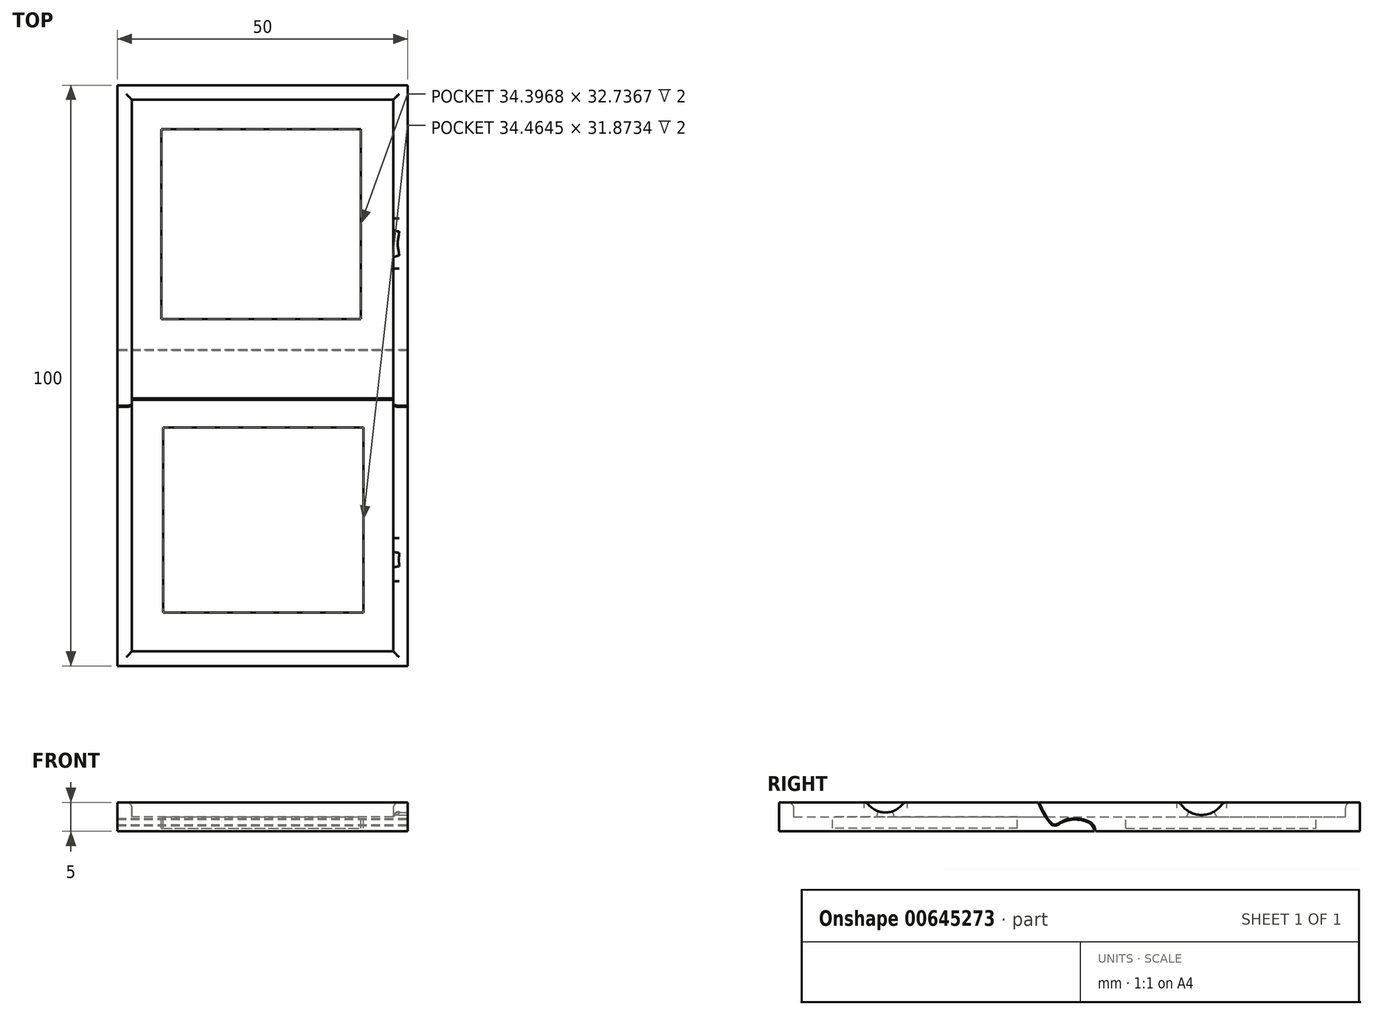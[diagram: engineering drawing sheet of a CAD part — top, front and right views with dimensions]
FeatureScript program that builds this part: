
annotation { "Feature Type Name" : "Feature", "Feature Type Description" : "" }
export const myFeature = defineFeature(function(context is Context, id is Id, definition is map)
    precondition{}
    {
        {
            var Q0;
            Q0=qCreatedBy(makeId("Front.planeOp"),FACE);
            var sketch = newSketch(context, id + "F0", { "sketchPlane" : qUnion([Q0])});
            skLineSegment(sketch, "E0.bottom", {"start": v(-50, 5) * mm, "end": v(0, 5) * mm});
            skLineSegment(sketch, "E0.top", {"start": v(-50, 0) * mm, "end": v(0, 0) * mm});
            skLineSegment(sketch, "E0.left", {"start": v(-50, 5) * mm, "end": v(-50, 0) * mm});
            skLineSegment(sketch, "E0.right", {"start": v(0, 5) * mm, "end": v(0, 0) * mm});
            skSolve(sketch);
        }
        {
            var Q0;
            Q0 = qSketchRegion(id + "F0", true);
            extrude(context, id + "F1", {"entities" : qUnion([Q0]), "endBound" : BoundingType.SYMMETRIC, "depth" : 100 * mm, "offsetDistance" : 25 * mm});
        }
        {
            var Q0;
            Q0=makeQuery(id+"F1.opExtrude","SWEPT_FACE",FACE,{"disambiguationData":[OSD([sQuery(id+"F0.wireOp",EDGE,"E0.bottom")])]});
            shell(context, id + "F2", {"entities" : qUnion([Q0]), "thickness" : 2.5 * mm});
        }
        {
            var Q0;
            Q0=makeQuery(id+"F1.opExtrude","SWEPT_FACE",FACE,{"disambiguationData":[OSD([sQuery(id+"F0.wireOp",EDGE,"E0.left")])]});
            var sketch = newSketch(context, id + "F3", { "sketchPlane" : qUnion([Q0])});
            skFitSpline(sketch, "E1", {"points": [v(-4.27, 0) * mm, v(0.38, 1.88) * mm, v(2.67, 1) * mm, v(5.4, 5) * mm], "startDerivative": vector(0, 15.13) * mm, "endDerivative": vector(6.53, 15.5) * mm});
            skFitSpline(sketch, "E2.0", {"points": [v(-4.45, 0) * mm, v(-4.45, 0.35) * mm, v(-4.26, 0.97) * mm, v(-3.57, 1.62) * mm, v(-2.63, 2.02) * mm, v(-1.56, 2.21) * mm, v(-0.48, 2.23) * mm, v(0.5, 2.07) * mm, v(1.25, 1.76) * mm, v(1.72, 1.48) * mm, v(2.04, 1.3) * mm, v(2.25, 1.2) * mm, v(2.43, 1.16) * mm, v(2.59, 1.15) * mm, v(2.76, 1.2) * mm, v(2.96, 1.32) * mm, v(3.18, 1.51) * mm, v(3.48, 1.84) * mm, v(3.88, 2.38) * mm, v(4.36, 3.2) * mm, v(4.82, 4.1) * mm, v(5.1, 4.75) * mm, v(5.24, 5.07) * mm]});
            skLineSegment(sketch, "E3", {"start": v(5.2, 5) * mm, "end": v(5.4, 5) * mm});
            skLineSegment(sketch, "E4", {"start": v(-4.45, 0) * mm, "end": v(-4.27, 0) * mm});
            skSolve(sketch);
        }
        {
            var Q0;
            Q0 = qSketchRegion(id + "F3", true);
            extrude(context, id + "F4", {"entities" : qUnion([Q0]), "operationType" : NewBodyOperationType.REMOVE, "oppositeDirection" : true, "depth" : 100 * mm, "offsetDistance" : 25 * mm});
        }
        {
            var Q0;
            {var subQ2=sQuery(id+"F0.wireOp",EDGE,"E0.top");Q0=makeQuery(id+"F4.boolean.opBoolean","SPLIT",FACE,{"disambiguationData":[TD([makeQuery(id+"F4.opExtrude","SWEPT_FACE",FACE,{"disambiguationData":[OSD([sQuery(id+"F3.wireOp",EDGE,"E1")])]})])],"derivedFrom":makeQuery(id+"F2.opShell","OFFSET_FACE",FACE,{"disambiguationData":[OSD([subQ2])]})});}
            var sketch = newSketch(context, id + "F5", { "sketchPlane" : qUnion([Q0])});
            skLineSegment(sketch, "E5.bottom", {"start": v(-42.12, -8.95) * mm, "end": v(-7.66, -8.95) * mm});
            skLineSegment(sketch, "E5.top", {"start": v(-42.12, -40.83) * mm, "end": v(-7.66, -40.83) * mm});
            skLineSegment(sketch, "E5.left", {"start": v(-42.12, -8.95) * mm, "end": v(-42.12, -40.83) * mm});
            skLineSegment(sketch, "E5.right", {"start": v(-7.66, -8.95) * mm, "end": v(-7.66, -40.83) * mm});
            skSolve(sketch);
        }
        {
            var Q0;
            Q0 = qSketchRegion(id + "F5", true);
            extrude(context, id + "F6", {"entities" : qUnion([Q0]), "operationType" : NewBodyOperationType.REMOVE, "oppositeDirection" : true, "depth" : 2 * mm, "offsetDistance" : 25 * mm});
        }
        {
            var Q0;
            Q0=makeQuery(id+"F6.boolean.opBoolean","COPY",EDGE,{"derivedFrom":makeQuery(id+"F6.opExtrude","CAP_EDGE",EDGE,{"disambiguationData":[OSD([sQuery(id+"F5.wireOp",EDGE,"E5.left")])],"isStart":true})});
            var Q1;
            Q1=makeQuery(id+"F6.boolean.opBoolean","COPY",EDGE,{"derivedFrom":makeQuery(id+"F6.opExtrude","CAP_EDGE",EDGE,{"disambiguationData":[OSD([sQuery(id+"F5.wireOp",EDGE,"E5.bottom")])],"isStart":true})});
            var Q2;
            Q2=makeQuery(id+"F6.boolean.opBoolean","COPY",EDGE,{"derivedFrom":makeQuery(id+"F6.opExtrude","CAP_EDGE",EDGE,{"disambiguationData":[OSD([sQuery(id+"F5.wireOp",EDGE,"E5.right")])],"isStart":true})});
            var Q3;
            Q3=makeQuery(id+"F6.boolean.opBoolean","COPY",EDGE,{"derivedFrom":makeQuery(id+"F6.opExtrude","CAP_EDGE",EDGE,{"disambiguationData":[OSD([sQuery(id+"F5.wireOp",EDGE,"E5.top")])],"isStart":true})});
            var Q4;
            {var subQ0=sQuery(id+"F0.wireOp",EDGE,"E0.bottom");var subQ2=sQuery(id+"F0.wireOp",EDGE,"E0.left");Q4=makeQuery(id+"F4.boolean.opBoolean","SPLIT",EDGE,{"disambiguationData":[TD([makeQuery(id+"F4.opExtrude","SWEPT_FACE",FACE,{"disambiguationData":[OSD([sQuery(id+"F3.wireOp",EDGE,"E1")])]})])],"derivedFrom":makeQuery(id+"F2.opShell","OFFSET_EDGE",EDGE,{"disambiguationData":[OSD([subQ0,subQ2])]})});}
            var Q5;
            {var subQ0=sQuery(id+"F0.wireOp",EDGE,"E0.bottom");Q5=makeQuery(id+"F2.opShell","OFFSET_EDGE",EDGE,{"disambiguationData":[OSD([subQ0]),TDD([makeQuery(id+"F1.opExtrude","CAP_EDGE",EDGE,{"disambiguationData":[OSD([subQ0])],"isStart":false})])]});}
            var Q6;
            {var subQ0=sQuery(id+"F0.wireOp",EDGE,"E0.bottom");var subQ1=sQuery(id+"F0.wireOp",EDGE,"E0.right");Q6=makeQuery(id+"F4.boolean.opBoolean","SPLIT",EDGE,{"disambiguationData":[TD([makeQuery(id+"F4.opExtrude","SWEPT_FACE",FACE,{"disambiguationData":[OSD([sQuery(id+"F3.wireOp",EDGE,"E1")])]})])],"derivedFrom":makeQuery(id+"F2.opShell","OFFSET_EDGE",EDGE,{"disambiguationData":[OSD([subQ0,subQ1])]})});}
            fillet(context, id + "F7", {"entities" : qUnion([Q0, Q1, Q2, Q3, Q4, Q5, Q6]), "radius" : 1 * mm, "tangentPropagation" : true, "allowEdgeOverflow" : false});
        }
        {
            var Q0;
            {var subQ2=sQuery(id+"F0.wireOp",EDGE,"E0.top");Q0=makeQuery(id+"F4.boolean.opBoolean","SPLIT",FACE,{"disambiguationData":[TD([makeQuery(id+"F4.opExtrude","SWEPT_FACE",FACE,{"disambiguationData":[OSD([sQuery(id+"F3.wireOp",EDGE,"E2.0")])]})])],"derivedFrom":makeQuery(id+"F2.opShell","OFFSET_FACE",FACE,{"disambiguationData":[OSD([subQ2])]})});}
            var sketch = newSketch(context, id + "F8", { "sketchPlane" : qUnion([Q0])});
            skLineSegment(sketch, "E6.bottom", {"start": v(-42.46, 9.72) * mm, "end": v(-8.06, 9.72) * mm});
            skLineSegment(sketch, "E6.top", {"start": v(-42.46, 42.45) * mm, "end": v(-8.06, 42.45) * mm});
            skLineSegment(sketch, "E6.left", {"start": v(-42.46, 9.72) * mm, "end": v(-42.46, 42.45) * mm});
            skLineSegment(sketch, "E6.right", {"start": v(-8.06, 9.72) * mm, "end": v(-8.06, 42.45) * mm});
            skSolve(sketch);
        }
        {
            var Q0;
            Q0=makeQuery(id+"F8.imprint","IMPRINT",FACE,{"disambiguationData":[TD([[makeQuery(id+"F8.imprint","IMPRINT",EDGE,{"derivedFrom":sQuery(id+"F8.wireOp",EDGE,"E6.bottom")}),1.0]])]});
            extrude(context, id + "F9", {"entities" : qUnion([Q0]), "operationType" : NewBodyOperationType.REMOVE, "oppositeDirection" : true, "depth" : 2 * mm, "offsetDistance" : 25 * mm});
        }
        {
            var Q0;
            Q0=makeQuery(id+"F9.boolean.opBoolean","COPY",EDGE,{"derivedFrom":makeQuery(id+"F9.opExtrude","CAP_EDGE",EDGE,{"disambiguationData":[OSD([sQuery(id+"F8.wireOp",EDGE,"E6.left")])],"isStart":true})});
            var Q1;
            Q1=makeQuery(id+"F9.boolean.opBoolean","COPY",EDGE,{"derivedFrom":makeQuery(id+"F9.opExtrude","CAP_EDGE",EDGE,{"disambiguationData":[OSD([sQuery(id+"F8.wireOp",EDGE,"E6.right")])],"isStart":true})});
            var Q2;
            Q2=makeQuery(id+"F9.boolean.opBoolean","COPY",EDGE,{"derivedFrom":makeQuery(id+"F9.opExtrude","CAP_EDGE",EDGE,{"disambiguationData":[OSD([sQuery(id+"F8.wireOp",EDGE,"E6.top")])],"isStart":true})});
            var Q3;
            {var subQ0=sQuery(id+"F0.wireOp",EDGE,"E0.bottom");var subQ2=sQuery(id+"F0.wireOp",EDGE,"E0.left");Q3=makeQuery(id+"F4.boolean.opBoolean","SPLIT",EDGE,{"disambiguationData":[TD([makeQuery(id+"F4.opExtrude","SWEPT_FACE",FACE,{"disambiguationData":[OSD([sQuery(id+"F3.wireOp",EDGE,"E2.0")])]})])],"derivedFrom":makeQuery(id+"F2.opShell","OFFSET_EDGE",EDGE,{"disambiguationData":[OSD([subQ0,subQ2])]})});}
            var Q4;
            {var subQ0=sQuery(id+"F0.wireOp",EDGE,"E0.bottom");Q4=makeQuery(id+"F2.opShell","OFFSET_EDGE",EDGE,{"disambiguationData":[OSD([subQ0]),TDD([makeQuery(id+"F1.opExtrude","CAP_EDGE",EDGE,{"disambiguationData":[OSD([subQ0])],"isStart":true})])]});}
            var Q5;
            {var subQ0=sQuery(id+"F0.wireOp",EDGE,"E0.bottom");var subQ1=sQuery(id+"F0.wireOp",EDGE,"E0.right");Q5=makeQuery(id+"F4.boolean.opBoolean","SPLIT",EDGE,{"disambiguationData":[TD([makeQuery(id+"F4.opExtrude","SWEPT_FACE",FACE,{"disambiguationData":[OSD([sQuery(id+"F3.wireOp",EDGE,"E2.0")])]})])],"derivedFrom":makeQuery(id+"F2.opShell","OFFSET_EDGE",EDGE,{"disambiguationData":[OSD([subQ0,subQ1])]})});}
            var Q6;
            Q6=makeQuery(id+"F9.boolean.opBoolean","COPY",EDGE,{"derivedFrom":makeQuery(id+"F9.opExtrude","CAP_EDGE",EDGE,{"disambiguationData":[OSD([sQuery(id+"F8.wireOp",EDGE,"E6.bottom")])],"isStart":true})});
            fillet(context, id + "F10", {"entities" : qUnion([Q0, Q1, Q2, Q3, Q4, Q5, Q6]), "radius" : 1 * mm, "tangentPropagation" : true, "allowEdgeOverflow" : false});
        }
        {
            var Q0;
            {var subQ1=sQuery(id+"F0.wireOp",EDGE,"E0.right");Q0=makeQuery(id+"F4.boolean.opBoolean","SPLIT",FACE,{"disambiguationData":[TD([makeQuery(id+"F4.opExtrude","SWEPT_FACE",FACE,{"disambiguationData":[OSD([sQuery(id+"F3.wireOp",EDGE,"E2.0")])]})])],"derivedFrom":makeQuery(id+"F1.opExtrude","SWEPT_FACE",FACE,{"disambiguationData":[OSD([subQ1])]})});}
            var sketch = newSketch(context, id + "F11", { "sketchPlane" : qUnion([Q0])});
            skArc(sketch, "E7.0", {"start": v(18.97, 5) * mm, "mid": v(22.73, 2.83) * mm, "end": v(26.5, 5) * mm});
            skLineSegment(sketch, "E8", {"start": v(18.97, 5) * mm, "end": v(26.5, 5) * mm});
            skSolve(sketch);
        }
        {
            var Q0;
            Q0=makeQuery(id+"F11.imprint","IMPRINT",FACE,{"disambiguationData":[TD([[makeQuery(id+"F11.imprint","IMPRINT",EDGE,{"derivedFrom":sQuery(id+"F11.wireOp",EDGE,"E7.0")}),1.0]])]});
            extrude(context, id + "F12", {"entities" : qUnion([Q0]), "operationType" : NewBodyOperationType.REMOVE, "oppositeDirection" : true, "depth" : 5 * mm, "offsetDistance" : 25 * mm});
        }
        {
            var Q0;
            Q0=makeQuery(id+"F12.boolean.opBoolean","INTERSECT",EDGE,{"disambiguationData":[OD(0.0)],"derivedFrom":[makeQuery(id+"F10.opFillet","BLEND_FACE",FACE,{"disambiguationData":[OSD([sQuery(id+"F0.wireOp",EDGE,"E0.bottom"),sQuery(id+"F0.wireOp",EDGE,"E0.right")])]}),makeQuery(id+"F12.opExtrude","SWEPT_FACE",FACE,{"disambiguationData":[OSD([sQuery(id+"F11.wireOp",EDGE,"E7.0")])]})]});
            var Q1;
            {var subQ1=sQuery(id+"F0.wireOp",EDGE,"E0.right");Q1=makeQuery(id+"F12.boolean.opBoolean","INTERSECT",EDGE,{"derivedFrom":[makeQuery(id+"F4.boolean.opBoolean","SPLIT",FACE,{"disambiguationData":[TD([makeQuery(id+"F4.opExtrude","SWEPT_FACE",FACE,{"disambiguationData":[OSD([sQuery(id+"F3.wireOp",EDGE,"E2.0")])]})])],"derivedFrom":makeQuery(id+"F2.opShell","OFFSET_FACE",FACE,{"disambiguationData":[OSD([subQ1])]})}),makeQuery(id+"F12.opExtrude","SWEPT_FACE",FACE,{"disambiguationData":[OSD([sQuery(id+"F11.wireOp",EDGE,"E7.0")])]})]});}
            var Q2;
            Q2=makeQuery(id+"F12.boolean.opBoolean","INTERSECT",EDGE,{"disambiguationData":[OD(1.0)],"derivedFrom":[makeQuery(id+"F10.opFillet","BLEND_FACE",FACE,{"disambiguationData":[OSD([sQuery(id+"F0.wireOp",EDGE,"E0.bottom"),sQuery(id+"F0.wireOp",EDGE,"E0.right")])]}),makeQuery(id+"F12.opExtrude","SWEPT_FACE",FACE,{"disambiguationData":[OSD([sQuery(id+"F11.wireOp",EDGE,"E7.0")])]})]});
            var Q3;
            {var subQ0=sQuery(id+"F11.wireOp",EDGE,"E8");var subQ1=sQuery(id+"F11.wireOp",EDGE,"E7.0");var subQ2=sQuery(id+"F0.wireOp",EDGE,"E0.bottom");var subQ3=sQuery(id+"F0.wireOp",EDGE,"E0.right");Q3=makeQuery(id+"F12.boolean.opBoolean","COPY",EDGE,{"derivedFrom":makeQuery(id+"F12.opExtrude","SWEPT_EDGE",EDGE,{"disambiguationData":[OSD([subQ2,subQ3,subQ1,subQ0]),TDD([makeQuery(id+"F11.imprint","INTERSECT",VERTEX,{"disambiguationData":[OD(1.0)],"derivedFrom":[makeQuery(id+"F4.boolean.opBoolean","SPLIT",EDGE,{"disambiguationData":[TD([makeQuery(id+"F4.opExtrude","SWEPT_FACE",FACE,{"disambiguationData":[OSD([sQuery(id+"F3.wireOp",EDGE,"E2.0")])]})])],"derivedFrom":makeQuery(id+"F1.opExtrude","SWEPT_EDGE",EDGE,{"disambiguationData":[OSD([subQ2,subQ3])]})}),subQ1,subQ0]})])]})});}
            var Q4;
            {var subQ0=sQuery(id+"F11.wireOp",EDGE,"E8");var subQ1=sQuery(id+"F11.wireOp",EDGE,"E7.0");var subQ2=sQuery(id+"F0.wireOp",EDGE,"E0.bottom");var subQ3=sQuery(id+"F0.wireOp",EDGE,"E0.right");Q4=makeQuery(id+"F12.boolean.opBoolean","COPY",EDGE,{"derivedFrom":makeQuery(id+"F12.opExtrude","SWEPT_EDGE",EDGE,{"disambiguationData":[OSD([subQ2,subQ3,subQ1,subQ0]),TDD([makeQuery(id+"F11.imprint","INTERSECT",VERTEX,{"disambiguationData":[OD(0.0)],"derivedFrom":[makeQuery(id+"F4.boolean.opBoolean","SPLIT",EDGE,{"disambiguationData":[TD([makeQuery(id+"F4.opExtrude","SWEPT_FACE",FACE,{"disambiguationData":[OSD([sQuery(id+"F3.wireOp",EDGE,"E2.0")])]})])],"derivedFrom":makeQuery(id+"F1.opExtrude","SWEPT_EDGE",EDGE,{"disambiguationData":[OSD([subQ2,subQ3])]})}),subQ1,subQ0]})])]})});}
            fillet(context, id + "F13", {"entities" : qUnion([Q0, Q1, Q2, Q3, Q4]), "radius" : 1 * mm, "tangentPropagation" : true, "allowEdgeOverflow" : false});
        }
        {
            var Q0;
            {var subQ1=sQuery(id+"F0.wireOp",EDGE,"E0.right");Q0=makeQuery(id+"F4.boolean.opBoolean","SPLIT",FACE,{"disambiguationData":[TD([makeQuery(id+"F4.opExtrude","SWEPT_FACE",FACE,{"disambiguationData":[OSD([sQuery(id+"F3.wireOp",EDGE,"E1")])]})])],"derivedFrom":makeQuery(id+"F1.opExtrude","SWEPT_FACE",FACE,{"disambiguationData":[OSD([subQ1])]})});}
            var sketch = newSketch(context, id + "F14", { "sketchPlane" : qUnion([Q0])});
            skArc(sketch, "E9", {"start": v(-34.92, 5) * mm, "mid": v(-31.7, 3.26) * mm, "end": v(-28.49, 5) * mm});
            skLineSegment(sketch, "E10", {"start": v(-34.92, 5) * mm, "end": v(-28.49, 5) * mm});
            skSolve(sketch);
        }
        {
            var Q0;
            Q0 = qSketchRegion(id + "F14", true);
            extrude(context, id + "F15", {"entities" : qUnion([Q0]), "operationType" : NewBodyOperationType.REMOVE, "oppositeDirection" : true, "depth" : 4 * mm, "offsetDistance" : 25 * mm});
        }
        {
            var Q0;
            {var subQ0=sQuery(id+"F14.wireOp",EDGE,"E10");var subQ1=sQuery(id+"F14.wireOp",EDGE,"E9");var subQ2=sQuery(id+"F0.wireOp",EDGE,"E0.bottom");var subQ3=sQuery(id+"F0.wireOp",EDGE,"E0.right");Q0=makeQuery(id+"F15.boolean.opBoolean","COPY",EDGE,{"derivedFrom":makeQuery(id+"F15.opExtrude","SWEPT_EDGE",EDGE,{"disambiguationData":[OSD([subQ2,subQ3,subQ1,subQ0]),TDD([makeQuery(id+"F14.imprint","INTERSECT",VERTEX,{"disambiguationData":[OD(0.0)],"derivedFrom":[makeQuery(id+"F4.boolean.opBoolean","SPLIT",EDGE,{"disambiguationData":[TD([makeQuery(id+"F4.opExtrude","SWEPT_FACE",FACE,{"disambiguationData":[OSD([sQuery(id+"F3.wireOp",EDGE,"E1")])]})])],"derivedFrom":makeQuery(id+"F1.opExtrude","SWEPT_EDGE",EDGE,{"disambiguationData":[OSD([subQ2,subQ3])]})}),subQ1,subQ0]})])]})});}
            var Q1;
            Q1=makeQuery(id+"F15.boolean.opBoolean","INTERSECT",EDGE,{"disambiguationData":[OD(0.0)],"derivedFrom":[makeQuery(id+"F7.opFillet","BLEND_FACE",FACE,{"disambiguationData":[OSD([sQuery(id+"F0.wireOp",EDGE,"E0.bottom"),sQuery(id+"F0.wireOp",EDGE,"E0.right")])]}),makeQuery(id+"F15.opExtrude","SWEPT_FACE",FACE,{"disambiguationData":[OSD([sQuery(id+"F14.wireOp",EDGE,"E9")])]})]});
            var Q2;
            {var subQ1=sQuery(id+"F0.wireOp",EDGE,"E0.right");Q2=makeQuery(id+"F15.boolean.opBoolean","INTERSECT",EDGE,{"derivedFrom":[makeQuery(id+"F4.boolean.opBoolean","SPLIT",FACE,{"disambiguationData":[TD([makeQuery(id+"F4.opExtrude","SWEPT_FACE",FACE,{"disambiguationData":[OSD([sQuery(id+"F3.wireOp",EDGE,"E1")])]})])],"derivedFrom":makeQuery(id+"F2.opShell","OFFSET_FACE",FACE,{"disambiguationData":[OSD([subQ1])]})}),makeQuery(id+"F15.opExtrude","SWEPT_FACE",FACE,{"disambiguationData":[OSD([sQuery(id+"F14.wireOp",EDGE,"E9")])]})]});}
            var Q3;
            Q3=makeQuery(id+"F15.boolean.opBoolean","INTERSECT",EDGE,{"disambiguationData":[OD(1.0)],"derivedFrom":[makeQuery(id+"F7.opFillet","BLEND_FACE",FACE,{"disambiguationData":[OSD([sQuery(id+"F0.wireOp",EDGE,"E0.bottom"),sQuery(id+"F0.wireOp",EDGE,"E0.right")])]}),makeQuery(id+"F15.opExtrude","SWEPT_FACE",FACE,{"disambiguationData":[OSD([sQuery(id+"F14.wireOp",EDGE,"E9")])]})]});
            var Q4;
            {var subQ0=sQuery(id+"F14.wireOp",EDGE,"E10");var subQ1=sQuery(id+"F14.wireOp",EDGE,"E9");var subQ2=sQuery(id+"F0.wireOp",EDGE,"E0.bottom");var subQ3=sQuery(id+"F0.wireOp",EDGE,"E0.right");Q4=makeQuery(id+"F15.boolean.opBoolean","COPY",EDGE,{"derivedFrom":makeQuery(id+"F15.opExtrude","SWEPT_EDGE",EDGE,{"disambiguationData":[OSD([subQ2,subQ3,subQ1,subQ0]),TDD([makeQuery(id+"F14.imprint","INTERSECT",VERTEX,{"disambiguationData":[OD(1.0)],"derivedFrom":[makeQuery(id+"F4.boolean.opBoolean","SPLIT",EDGE,{"disambiguationData":[TD([makeQuery(id+"F4.opExtrude","SWEPT_FACE",FACE,{"disambiguationData":[OSD([sQuery(id+"F3.wireOp",EDGE,"E1")])]})])],"derivedFrom":makeQuery(id+"F1.opExtrude","SWEPT_EDGE",EDGE,{"disambiguationData":[OSD([subQ2,subQ3])]})}),subQ1,subQ0]})])]})});}
            fillet(context, id + "F16", {"entities" : qUnion([Q0, Q1, Q2, Q3, Q4]), "radius" : 1 * mm, "tangentPropagation" : true, "allowEdgeOverflow" : false});
        }
    });
